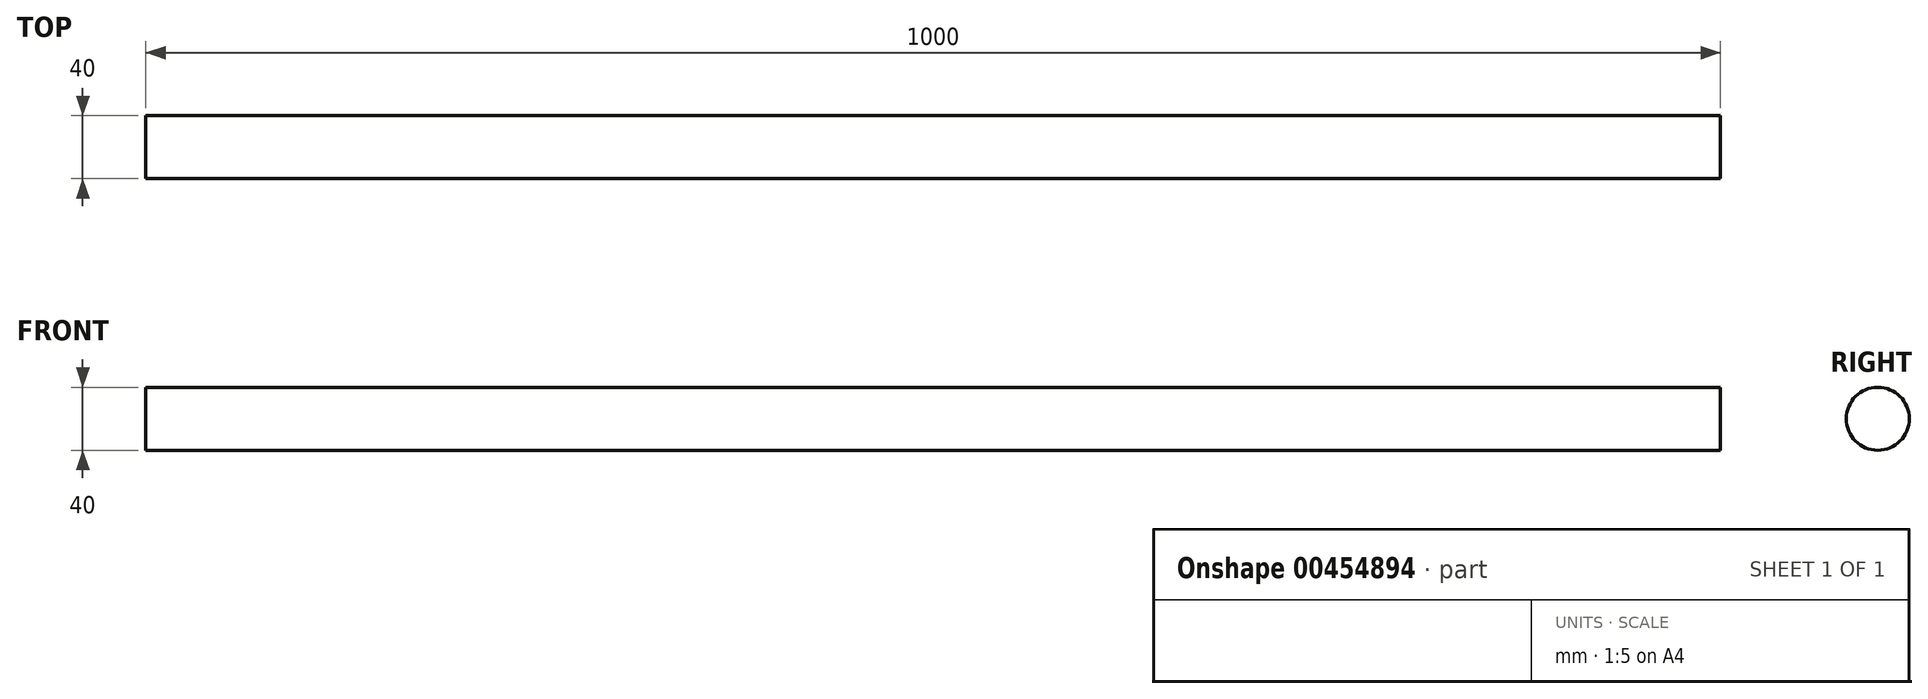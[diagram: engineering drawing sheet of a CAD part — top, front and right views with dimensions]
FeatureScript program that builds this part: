
annotation { "Feature Type Name" : "Feature", "Feature Type Description" : "" }
export const myFeature = defineFeature(function(context is Context, id is Id, definition is map)
    precondition{}
    {
        {
            var Q0;
            Q0=qCreatedBy(makeId("Right.planeOp"),FACE);
            var sketch = newSketch(context, id + "F0", { "sketchPlane" : qUnion([Q0])});
            skCircle(sketch, "E0", {"center": v(0, 0) * mm, "radius": 20 * mm});
            skSolve(sketch);
        }
        {
            var Q0;
            Q0 = qSketchRegion(id + "F0", true);
            extrude(context, id + "F1", {"entities" : qUnion([Q0]), "depth" : 1000 * mm});
        }
    });
